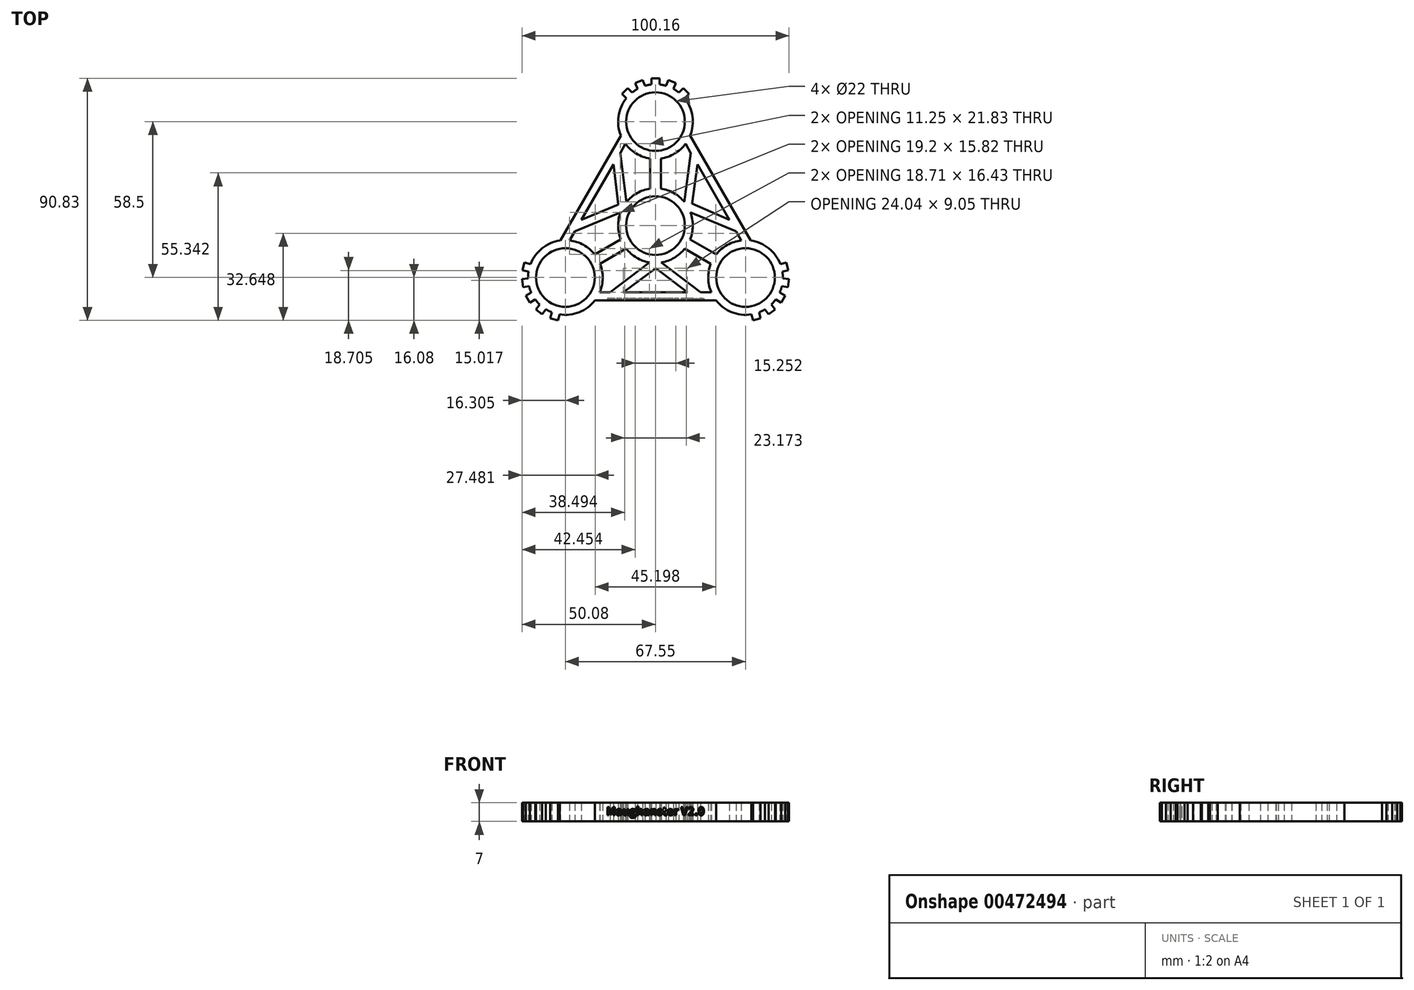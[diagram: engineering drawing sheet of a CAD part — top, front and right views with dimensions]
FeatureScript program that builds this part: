
annotation { "Feature Type Name" : "Feature", "Feature Type Description" : "" }
export const myFeature = defineFeature(function(context is Context, id is Id, definition is map)
    precondition{}
    {
        {
            var Q0;
            Q0=qCreatedBy(makeId("Top.planeOp"),FACE);
            var sketch = newSketch(context, id + "F0", { "sketchPlane" : qUnion([Q0])});
            skCircle(sketch, "E0", {"center": v(0, 0) * mm, "radius": 11 * mm});
            skArc(sketch, "E1.0", {"start": v(-2, 13.86) * mm, "mid": v(-6.9, 12.18) * mm, "end": v(-10.85, 8.84) * mm});
            skCircle(sketch, "E2", {"center": v(0, 39) * mm, "radius": 11 * mm});
            skArc(sketch, "E3.0", {"start": v(-10.9, 47.78) * mm, "mid": v(-13.85, 41.03) * mm, "end": v(-12.97, 33.72) * mm});
            skLineSegment(sketch, "E4", {"start": v(0, 11) * mm, "end": v(0, 28) * mm, "construction": true});
            skLineSegment(sketch, "E5.0", {"start": v(2, 13.86) * mm, "end": v(2, 25.14) * mm});
            skLineSegment(sketch, "E6.0", {"start": v(-2, 13.86) * mm, "end": v(-2, 25.14) * mm});
            skLineSegment(sketch, "E7", {"start": v(0, 53) * mm, "end": v(0, 55) * mm, "construction": true});
            skLineSegment(sketch, "E8.0", {"start": v(1.5, 52.92) * mm, "end": v(1.5, 55.25) * mm});
            skLineSegment(sketch, "E9.0", {"start": v(-1.5, 52.92) * mm, "end": v(-1.5, 55.25) * mm});
            skLineSegment(sketch, "E10", {"start": v(-1.5, 55.25) * mm, "end": v(1.5, 55.25) * mm});
            skLineSegment(sketch, "E11.1.0", {"start": v(4.83, 54.59) * mm, "end": v(7.6, 53.44) * mm});
            skLineSegment(sketch, "E11.1.1", {"start": v(3.94, 52.43) * mm, "end": v(4.83, 54.59) * mm});
            skLineSegment(sketch, "E11.1.2", {"start": v(6.71, 51.29) * mm, "end": v(7.6, 53.44) * mm});
            skLineSegment(sketch, "E11.2.0", {"start": v(10.43, 51.55) * mm, "end": v(12.55, 49.43) * mm});
            skLineSegment(sketch, "E11.2.1", {"start": v(8.78, 49.9) * mm, "end": v(10.43, 51.55) * mm});
            skLineSegment(sketch, "E11.2.2", {"start": v(10.9, 47.78) * mm, "end": v(12.55, 49.43) * mm});
            skLineSegment(sketch, "E11.anchor1", {"start": v(0, 39) * mm, "end": v(-1.5, 55.25) * mm, "construction": true});
            skLineSegment(sketch, "E11.anchor2", {"start": v(0, 39) * mm, "end": v(10.43, 51.55) * mm, "construction": true});
            skLineSegment(sketch, "E12.MirrorCS", {"start": v(-4.83, 54.59) * mm, "end": v(-7.6, 53.44) * mm});
            skLineSegment(sketch, "E13.MirrorCS", {"start": v(-3.94, 52.43) * mm, "end": v(-4.83, 54.59) * mm});
            skLineSegment(sketch, "E14.MirrorCS", {"start": v(-6.71, 51.29) * mm, "end": v(-7.6, 53.44) * mm});
            skLineSegment(sketch, "E15.MirrorCS", {"start": v(-8.78, 49.9) * mm, "end": v(-10.43, 51.55) * mm});
            skLineSegment(sketch, "E16.MirrorCS", {"start": v(-10.43, 51.55) * mm, "end": v(-12.55, 49.43) * mm});
            skLineSegment(sketch, "E17.MirrorCS", {"start": v(-10.9, 47.78) * mm, "end": v(-12.55, 49.43) * mm});
            skArc(sketch, "E18.trimOffspring", {"start": v(-6.71, 51.29) * mm, "mid": v(-7.78, 50.64) * mm, "end": v(-8.78, 49.9) * mm});
            skArc(sketch, "E19.trimOffspring", {"start": v(-1.29, 52.94) * mm, "mid": v(-2.63, 52.75) * mm, "end": v(-3.94, 52.43) * mm});
            skArc(sketch, "E20.trimOffspring", {"start": v(3.94, 52.43) * mm, "mid": v(2.73, 52.73) * mm, "end": v(1.5, 52.92) * mm});
            skArc(sketch, "E21.trimOffspring", {"start": v(8.95, 49.77) * mm, "mid": v(7.87, 50.58) * mm, "end": v(6.71, 51.29) * mm});
            skArc(sketch, "E22.trimOffspring", {"start": v(2, 25.14) * mm, "mid": v(7.18, 26.98) * mm, "end": v(11.26, 30.68) * mm});
            skLineSegment(sketch, "E23.1.0", {"start": v(-33.77, -19.5) * mm, "end": v(-47.1, -28.92) * mm, "construction": true});
            skPoint(sketch, "E23.1.1", {"position": v(-33.77, -19.5) * mm});
            skCircle(sketch, "E23.1.2", {"center": v(-33.77, -19.5) * mm, "radius": 11 * mm});
            skLineSegment(sketch, "E23.1.3", {"start": v(-9.53, -5.5) * mm, "end": v(-24.25, -14) * mm, "construction": true});
            skArc(sketch, "E23.1.4", {"start": v(-35.93, -33.33) * mm, "mid": v(-28.6, -32.51) * mm, "end": v(-22.72, -28.09) * mm});
            skLineSegment(sketch, "E23.1.5", {"start": v(-13, -5.2) * mm, "end": v(-22.77, -10.84) * mm});
            skLineSegment(sketch, "E23.1.6", {"start": v(-11, -8.66) * mm, "end": v(-20.77, -14.3) * mm});
            skLineSegment(sketch, "E23.1.7", {"start": v(-33.77, -19.5) * mm, "end": v(-49.86, -16.74) * mm, "construction": true});
            skArc(sketch, "E23.1.8", {"start": v(-22.77, -10.84) * mm, "mid": v(-26.96, -7.27) * mm, "end": v(-32.2, -5.59) * mm});
            skLineSegment(sketch, "E23.1.9", {"start": v(-41.06, -31.46) * mm, "end": v(-42.48, -33.3) * mm});
            skLineSegment(sketch, "E23.1.10", {"start": v(-35.93, -33.33) * mm, "end": v(-36.53, -35.58) * mm});
            skLineSegment(sketch, "E23.1.11", {"start": v(-49.86, -16.74) * mm, "end": v(-49.08, -13.85) * mm});
            skLineSegment(sketch, "E23.1.12", {"start": v(-47.77, -19.83) * mm, "end": v(-50.08, -20.13) * mm});
            skArc(sketch, "E23.1.13", {"start": v(-47.57, -17.13) * mm, "mid": v(-47.74, -18.48) * mm, "end": v(-47.77, -19.83) * mm});
            skLineSegment(sketch, "E23.1.14", {"start": v(-44.86, -31.48) * mm, "end": v(-42.48, -33.3) * mm});
            skLineSegment(sketch, "E23.1.15", {"start": v(-45.9, -26.5) * mm, "end": v(-47.63, -27.5) * mm, "construction": true});
            skLineSegment(sketch, "E23.1.16", {"start": v(-46.58, -25.16) * mm, "end": v(-48.6, -26.33) * mm});
            skLineSegment(sketch, "E23.1.17", {"start": v(-47.1, -28.92) * mm, "end": v(-48.6, -26.33) * mm});
            skLineSegment(sketch, "E23.1.18", {"start": v(-45.08, -27.76) * mm, "end": v(-47.1, -28.92) * mm});
            skLineSegment(sketch, "E23.1.19", {"start": v(-49.7, -23.1) * mm, "end": v(-50.08, -20.13) * mm});
            skLineSegment(sketch, "E23.1.20", {"start": v(-47.38, -22.8) * mm, "end": v(-49.7, -23.1) * mm});
            skArc(sketch, "E23.1.21", {"start": v(-47.38, -22.8) * mm, "mid": v(-47.03, -24) * mm, "end": v(-46.58, -25.16) * mm});
            skArc(sketch, "E23.1.22", {"start": v(-41.06, -31.46) * mm, "mid": v(-39.97, -32.06) * mm, "end": v(-38.83, -32.56) * mm});
            skLineSegment(sketch, "E23.1.23", {"start": v(-39.43, -34.8) * mm, "end": v(-36.53, -35.58) * mm});
            skLineSegment(sketch, "E23.1.24", {"start": v(-43.44, -29.63) * mm, "end": v(-44.86, -31.48) * mm});
            skLineSegment(sketch, "E23.1.25", {"start": v(-46.83, -14.45) * mm, "end": v(-49.08, -13.85) * mm});
            skArc(sketch, "E23.1.26", {"start": v(-45.2, -27.58) * mm, "mid": v(-44.37, -28.65) * mm, "end": v(-43.44, -29.63) * mm});
            skLineSegment(sketch, "E23.1.27", {"start": v(-38.83, -32.56) * mm, "end": v(-39.43, -34.8) * mm});
            skLineSegment(sketch, "E23.1.28", {"start": v(-47.6, -17.35) * mm, "end": v(-49.86, -16.74) * mm});
            skLineSegment(sketch, "E23.2.0", {"start": v(33.77, -19.5) * mm, "end": v(48.6, -26.33) * mm, "construction": true});
            skPoint(sketch, "E23.2.1", {"position": v(33.77, -19.5) * mm});
            skCircle(sketch, "E23.2.2", {"center": v(33.77, -19.5) * mm, "radius": 11 * mm});
            skLineSegment(sketch, "E23.2.3", {"start": v(9.53, -5.5) * mm, "end": v(24.25, -14) * mm, "construction": true});
            skArc(sketch, "E23.2.4", {"start": v(46.83, -14.45) * mm, "mid": v(42.46, -8.52) * mm, "end": v(35.69, -5.63) * mm});
            skLineSegment(sketch, "E23.2.5", {"start": v(11, -8.66) * mm, "end": v(20.77, -14.3) * mm});
            skLineSegment(sketch, "E23.2.6", {"start": v(13, -5.2) * mm, "end": v(22.77, -10.84) * mm});
            skLineSegment(sketch, "E23.2.7", {"start": v(33.77, -19.5) * mm, "end": v(39.43, -34.8) * mm, "construction": true});
            skArc(sketch, "E23.2.8", {"start": v(20.77, -14.3) * mm, "mid": v(19.78, -19.71) * mm, "end": v(20.94, -25.09) * mm});
            skLineSegment(sketch, "E23.2.9", {"start": v(47.77, -19.83) * mm, "end": v(50.08, -20.13) * mm});
            skLineSegment(sketch, "E23.2.10", {"start": v(46.83, -14.45) * mm, "end": v(49.08, -13.85) * mm});
            skLineSegment(sketch, "E23.2.11", {"start": v(39.43, -34.8) * mm, "end": v(36.53, -35.58) * mm});
            skLineSegment(sketch, "E23.2.12", {"start": v(41.06, -31.46) * mm, "end": v(42.48, -33.3) * mm});
            skArc(sketch, "E23.2.13", {"start": v(38.63, -32.63) * mm, "mid": v(39.87, -32.1) * mm, "end": v(41.06, -31.46) * mm});
            skLineSegment(sketch, "E23.2.14", {"start": v(49.7, -23.1) * mm, "end": v(50.08, -20.13) * mm});
            skLineSegment(sketch, "E23.2.15", {"start": v(45.9, -26.5) * mm, "end": v(47.63, -27.5) * mm, "construction": true});
            skLineSegment(sketch, "E23.2.16", {"start": v(45.08, -27.76) * mm, "end": v(47.1, -28.92) * mm});
            skLineSegment(sketch, "E23.2.17", {"start": v(48.6, -26.33) * mm, "end": v(47.1, -28.92) * mm});
            skLineSegment(sketch, "E23.2.18", {"start": v(46.58, -25.16) * mm, "end": v(48.6, -26.33) * mm});
            skLineSegment(sketch, "E23.2.19", {"start": v(44.86, -31.48) * mm, "end": v(42.48, -33.3) * mm});
            skLineSegment(sketch, "E23.2.20", {"start": v(43.44, -29.63) * mm, "end": v(44.86, -31.48) * mm});
            skArc(sketch, "E23.2.21", {"start": v(43.44, -29.63) * mm, "mid": v(44.3, -28.73) * mm, "end": v(45.08, -27.76) * mm});
            skArc(sketch, "E23.2.22", {"start": v(47.77, -19.83) * mm, "mid": v(47.75, -18.58) * mm, "end": v(47.6, -17.35) * mm});
            skLineSegment(sketch, "E23.2.23", {"start": v(49.86, -16.74) * mm, "end": v(49.08, -13.85) * mm});
            skLineSegment(sketch, "E23.2.24", {"start": v(47.38, -22.8) * mm, "end": v(49.7, -23.1) * mm});
            skLineSegment(sketch, "E23.2.25", {"start": v(35.93, -33.33) * mm, "end": v(36.53, -35.58) * mm});
            skArc(sketch, "E23.2.26", {"start": v(46.5, -25.36) * mm, "mid": v(47, -24.1) * mm, "end": v(47.38, -22.8) * mm});
            skLineSegment(sketch, "E23.2.27", {"start": v(47.6, -17.35) * mm, "end": v(49.86, -16.74) * mm});
            skLineSegment(sketch, "E23.2.28", {"start": v(38.83, -32.56) * mm, "end": v(39.43, -34.8) * mm});
            skArc(sketch, "E24.trimOffspring", {"start": v(13, -5.2) * mm, "mid": v(14, -0.12) * mm, "end": v(13.09, 4.98) * mm});
            skArc(sketch, "E25.trimOffspring", {"start": v(-11, -8.66) * mm, "mid": v(-7.1, -12.06) * mm, "end": v(-2.23, -13.82) * mm});
            skLineSegment(sketch, "E26", {"start": v(-12.97, 33.72) * mm, "end": v(-35.69, -5.63) * mm});
            skLineSegment(sketch, "E27.0", {"start": v(-11.26, 30.68) * mm, "end": v(-13.25, 27.23) * mm});
            skArc(sketch, "E28.trimOffspring", {"start": v(-11.26, 30.68) * mm, "mid": v(-7.18, 26.98) * mm, "end": v(-2, 25.14) * mm});
            skArc(sketch, "E29.trimOffspring", {"start": v(-35.69, -5.63) * mm, "mid": v(-42.46, -8.52) * mm, "end": v(-46.83, -14.45) * mm});
            skLineSegment(sketch, "E30", {"start": v(-12.12, 7) * mm, "end": v(-28.97, 0) * mm, "construction": true});
            skLineSegment(sketch, "E31", {"start": v(-12.12, 7) * mm, "end": v(-21.73, 12.54) * mm, "construction": true});
            skLineSegment(sketch, "E32.0", {"start": v(-13.98, 7.85) * mm, "end": v(-27.74, 2.14) * mm});
            skLineSegment(sketch, "E33.0", {"start": v(-13.09, 4.98) * mm, "end": v(-30.2, -2.14) * mm});
            skLineSegment(sketch, "E34.trimOffspring", {"start": v(-30.2, -2.14) * mm, "end": v(-32.2, -5.59) * mm});
            skArc(sketch, "E35.trimOffspring", {"start": v(-13.09, 4.98) * mm, "mid": v(-14, -0.12) * mm, "end": v(-13, -5.2) * mm});
            skLineSegment(sketch, "E36.MirrorCS", {"start": v(-10.85, 8.84) * mm, "end": v(-13.25, 27.23) * mm});
            skLineSegment(sketch, "E37.trimOffspring", {"start": v(-15.72, 22.95) * mm, "end": v(-27.74, 2.14) * mm});
            skPoint(sketch, "E38.orphan", {"position": v(-10.45, 9.32) * mm});
            skLineSegment(sketch, "E39.trimOffspring", {"start": v(-13.98, 7.85) * mm, "end": v(-15.72, 22.95) * mm});
            skPoint(sketch, "E40.MirrorCS.start.orphan", {"position": v(-13.3, 4.38) * mm});
            skLineSegment(sketch, "E41.1.0", {"start": v(-22.72, -28.09) * mm, "end": v(22.72, -28.09) * mm});
            skLineSegment(sketch, "E41.1.1", {"start": v(0.2, -16.04) * mm, "end": v(-12.02, -25.09) * mm});
            skLineSegment(sketch, "E41.1.2", {"start": v(0, -14) * mm, "end": v(0, -25.09) * mm, "construction": true});
            skLineSegment(sketch, "E41.1.3", {"start": v(-12.02, -25.09) * mm, "end": v(12.02, -25.09) * mm});
            skLineSegment(sketch, "E41.1.4", {"start": v(-2.23, -13.82) * mm, "end": v(-16.95, -25.09) * mm});
            skLineSegment(sketch, "E41.1.5", {"start": v(16.95, -25.09) * mm, "end": v(20.94, -25.09) * mm});
            skLineSegment(sketch, "E41.1.6", {"start": v(2.23, -13.82) * mm, "end": v(16.95, -25.09) * mm});
            skLineSegment(sketch, "E41.1.7", {"start": v(0.2, -16.04) * mm, "end": v(12.02, -25.09) * mm});
            skLineSegment(sketch, "E41.1.8", {"start": v(0, -14) * mm, "end": v(14.49, -25.09) * mm, "construction": true});
            skLineSegment(sketch, "E41.1.9", {"start": v(-20.94, -25.09) * mm, "end": v(-16.95, -25.09) * mm});
            skLineSegment(sketch, "E41.2.0", {"start": v(35.69, -5.63) * mm, "end": v(12.97, 33.72) * mm});
            skLineSegment(sketch, "E41.2.1", {"start": v(13.8, 8.18) * mm, "end": v(27.74, 2.14) * mm});
            skLineSegment(sketch, "E41.2.2", {"start": v(12.12, 7) * mm, "end": v(21.73, 12.54) * mm, "construction": true});
            skLineSegment(sketch, "E41.2.3", {"start": v(27.74, 2.14) * mm, "end": v(15.72, 22.95) * mm});
            skLineSegment(sketch, "E41.2.4", {"start": v(13.09, 4.98) * mm, "end": v(30.2, -2.14) * mm});
            skLineSegment(sketch, "E41.2.5", {"start": v(13.25, 27.23) * mm, "end": v(11.26, 30.68) * mm});
            skLineSegment(sketch, "E41.2.6", {"start": v(10.85, 8.84) * mm, "end": v(13.25, 27.23) * mm});
            skLineSegment(sketch, "E41.2.7", {"start": v(13.8, 8.18) * mm, "end": v(15.72, 22.95) * mm});
            skLineSegment(sketch, "E41.2.8", {"start": v(12.12, 7) * mm, "end": v(14.49, 25.09) * mm, "construction": true});
            skLineSegment(sketch, "E41.2.9", {"start": v(32.2, -5.59) * mm, "end": v(30.2, -2.14) * mm});
            skArc(sketch, "E42.trimOffspring", {"start": v(12.97, 33.72) * mm, "mid": v(13.85, 41.03) * mm, "end": v(10.9, 47.78) * mm});
            skArc(sketch, "E43.trimOffspring", {"start": v(32.2, -5.59) * mm, "mid": v(26.96, -7.27) * mm, "end": v(22.77, -10.84) * mm});
            skArc(sketch, "E44.trimOffspring", {"start": v(10.85, 8.84) * mm, "mid": v(6.9, 12.18) * mm, "end": v(2, 13.86) * mm});
            skArc(sketch, "E45.trimOffspring", {"start": v(2.23, -13.82) * mm, "mid": v(7.1, -12.06) * mm, "end": v(11, -8.66) * mm});
            skArc(sketch, "E46.trimOffspring", {"start": v(22.72, -28.09) * mm, "mid": v(28.6, -32.51) * mm, "end": v(35.93, -33.33) * mm});
            skArc(sketch, "E47.trimOffspring", {"start": v(-20.94, -25.09) * mm, "mid": v(-19.78, -19.71) * mm, "end": v(-20.77, -14.3) * mm});
            skSolve(sketch);
        }
        {
            var Q0;
            Q0=qSketchRegion(id+"F0",true);
            extrude(context, id + "F1", {"entities" : qUnion([Q0]), "depth" : 7 * mm});
        }
        {
            var Q0;
            Q0=makeQuery(id+"F1.opExtrude","SWEPT_FACE",FACE,{"disambiguationData":[OSD([sQuery(id+"F0.wireOp",EDGE,"E41.1.0")])]});
            var sketch = newSketch(context, id + "F2", { "sketchPlane" : qUnion([Q0])});
            skText(sketch, "E48", { "text": "Maughanster V2.0", "fontName": "NotoSansCJKkr-Bold.otf"});
            skPoint(sketch, "E49", {"position": v(-18.42, 3.8) * mm});
            const initialGuessF2  = {"E48": [-0.01842, 0.0023, 1, 0, 0.003]};
            skSetInitialGuess(sketch, initialGuessF2);
            skSolve(sketch);
        }
        {
            var Q0;
            Q0=qSketchRegion(id+"F2",true);
            extrude(context, id + "F3", {"entities" : qUnion([Q0]), "operationType" : NewBodyOperationType.REMOVE, "oppositeDirection" : true, "depth" : .75 * mm});
        }
    });
